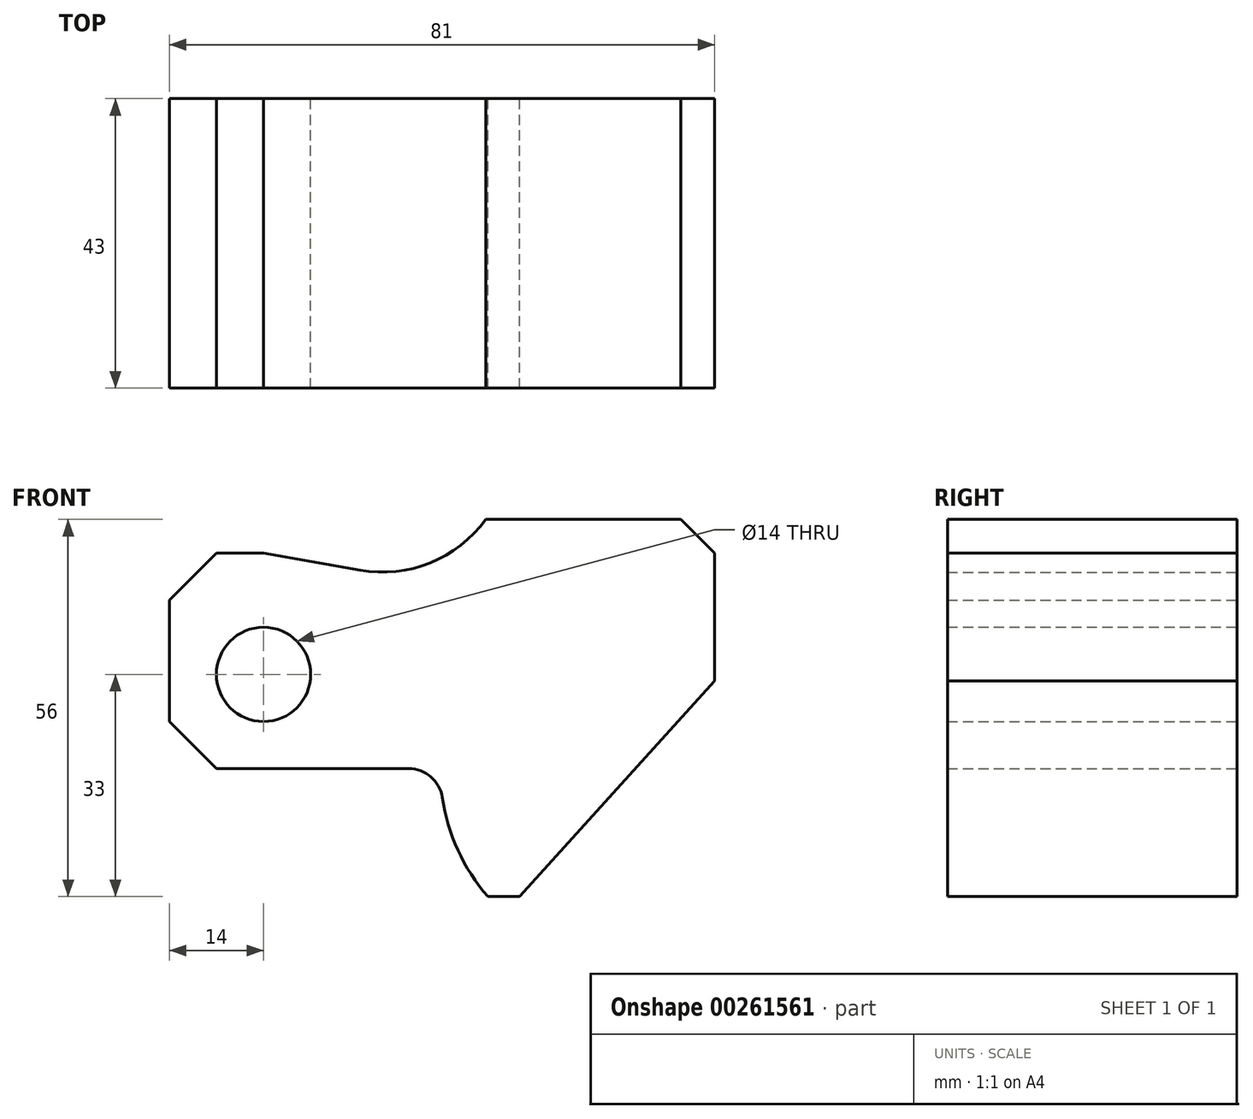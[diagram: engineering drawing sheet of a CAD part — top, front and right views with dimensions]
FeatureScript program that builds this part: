
annotation { "Feature Type Name" : "Feature", "Feature Type Description" : "" }
export const myFeature = defineFeature(function(context is Context, id is Id, definition is map)
    precondition{}
    {
        {
            var Q0;
            Q0=qCreatedBy(makeId("Front.planeOp"),FACE);
            var sketch = newSketch(context, id + "F0", { "sketchPlane" : qUnion([Q0])});
            skCircle(sketch, "E0", {"center": v(0, 0) * mm, "radius": 7 * mm});
            skLineSegment(sketch, "E1.bottom", {"start": v(-7, 18) * mm, "end": v(0, 18) * mm});
            skLineSegment(sketch, "E1.left", {"start": v(-14, 11) * mm, "end": v(-14, -7) * mm});
            skLineSegment(sketch, "E2", {"start": v(-14, 11) * mm, "end": v(-7, 18) * mm});
            skLineSegment(sketch, "E3", {"start": v(-14, -7) * mm, "end": v(-7, -14) * mm});
            skLineSegment(sketch, "E4", {"start": v(-14, 11) * mm, "end": v(-14, 18) * mm, "construction": true});
            skLineSegment(sketch, "E5", {"start": v(-14, 18) * mm, "end": v(-7, 18) * mm, "construction": true});
            skLineSegment(sketch, "E6", {"start": v(-14, -7) * mm, "end": v(-14, -13.84) * mm, "construction": true});
            skLineSegment(sketch, "E7", {"start": v(-14, -13.84) * mm, "end": v(-7, -14) * mm, "construction": true});
            skLineSegment(sketch, "E8", {"start": v(0, 0) * mm, "end": v(0, 18) * mm, "construction": true});
            skLineSegment(sketch, "E9", {"start": v(-7, -14) * mm, "end": v(21.59, -14) * mm});
            skArc(sketch, "E10", {"start": v(26.53, -18.26) * mm, "mid": v(24.85, -15.21) * mm, "end": v(21.59, -14) * mm});
            skLineSegment(sketch, "E11", {"start": v(0, 18) * mm, "end": v(14.34, 15.47) * mm});
            skArc(sketch, "E12", {"start": v(14.34, 15.47) * mm, "mid": v(24.75, 16.56) * mm, "end": v(33, 23) * mm});
            skLineSegment(sketch, "E13", {"start": v(33, 23) * mm, "end": v(62, 23) * mm});
            skLineSegment(sketch, "E14", {"start": v(62, 23) * mm, "end": v(67, 18) * mm});
            skLineSegment(sketch, "E15", {"start": v(67, 18) * mm, "end": v(67, 31.36) * mm, "construction": true});
            skLineSegment(sketch, "E16", {"start": v(0, 18) * mm, "end": v(8.67, 18) * mm, "construction": true});
            skLineSegment(sketch, "E17", {"start": v(38, -33) * mm, "end": v(33.3, -33) * mm});
            skArc(sketch, "E18", {"start": v(26.53, -18.26) * mm, "mid": v(28.87, -26.12) * mm, "end": v(33.3, -33) * mm});
            skLineSegment(sketch, "E19", {"start": v(67, 18) * mm, "end": v(67, -1) * mm});
            skLineSegment(sketch, "E20", {"start": v(67, -1) * mm, "end": v(38, -33) * mm});
            skSolve(sketch);
        }
        {
            var Q0;
            Q0 = qSketchRegion(id + "F0", true);
            extrude(context, id + "F1", {"entities" : qUnion([Q0]), "depth" : 43 * mm});
        }
    });
